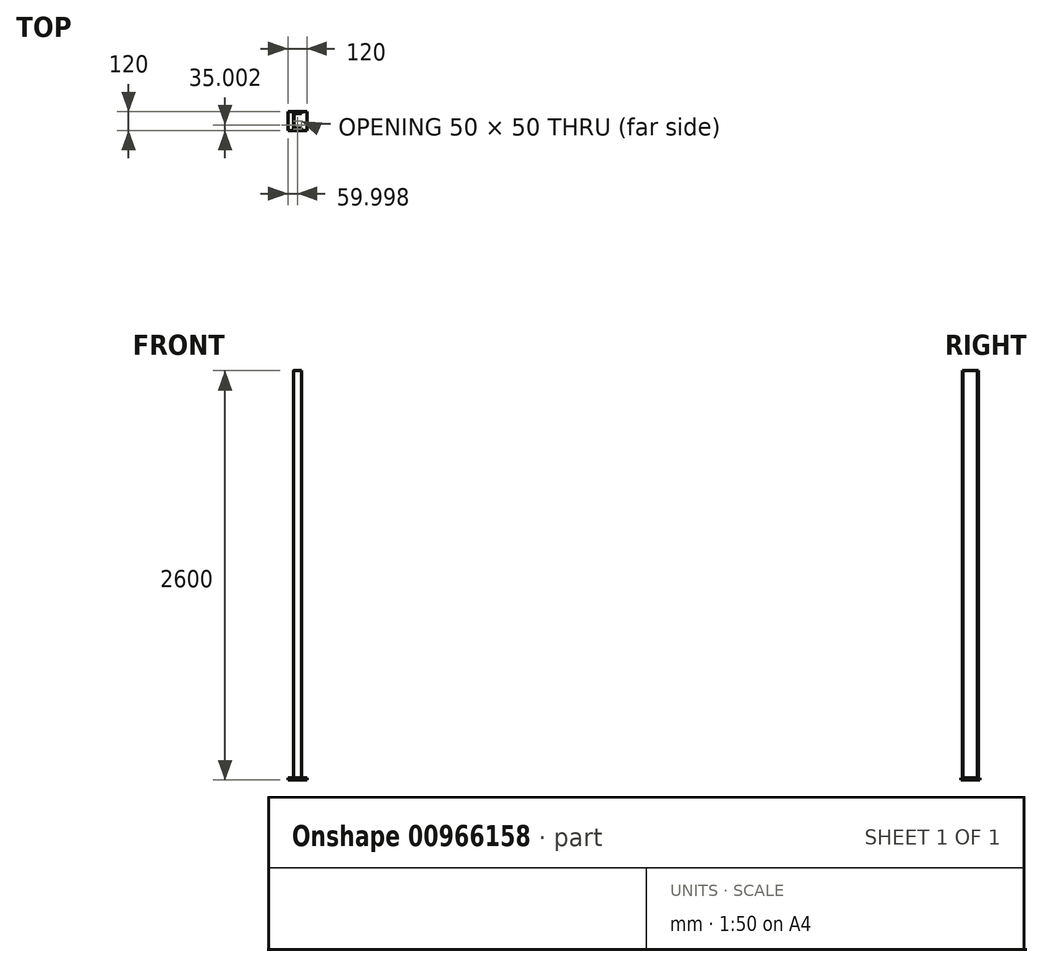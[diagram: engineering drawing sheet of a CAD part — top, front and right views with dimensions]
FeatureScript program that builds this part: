
annotation { "Feature Type Name" : "Feature", "Feature Type Description" : "" }
export const myFeature = defineFeature(function(context is Context, id is Id, definition is map)
    precondition{}
    {
        {
            var Q0;
            Q0=qCreatedBy(makeId("Top.planeOp"),FACE);
            var sketch = newSketch(context, id + "F0", { "sketchPlane" : qUnion([Q0])});
            skLineSegment(sketch, "E0.bottom", {"start": v(-5203.7, 5895.42) * mm, "end": v(-203.7, 5895.42) * mm});
            skLineSegment(sketch, "E0.top", {"start": v(-5203.7, -104.58) * mm, "end": v(-203.7, -104.58) * mm});
            skLineSegment(sketch, "E0.left", {"start": v(-5203.7, 5895.42) * mm, "end": v(-5203.7, -104.58) * mm});
            skLineSegment(sketch, "E0.right", {"start": v(-203.7, 5895.42) * mm, "end": v(-203.7, -104.58) * mm});
            skLineSegment(sketch, "E1.bottom", {"start": v(-5203.7, -104.58) * mm, "end": v(-5083.7, -104.58) * mm});
            skLineSegment(sketch, "E1.top", {"start": v(-5203.7, 15.42) * mm, "end": v(-5083.7, 15.42) * mm});
            skLineSegment(sketch, "E1.left", {"start": v(-5203.7, -104.58) * mm, "end": v(-5203.7, 15.42) * mm});
            skLineSegment(sketch, "E1.right", {"start": v(-5083.7, -104.58) * mm, "end": v(-5083.7, 15.42) * mm});
            skLineSegment(sketch, "E2", {"start": v(-5203.7, -44.58) * mm, "end": v(-5083.7, -44.58) * mm});
            skLineSegment(sketch, "E3", {"start": v(-5143.7, 5.42) * mm, "end": v(-5163.7, 5.42) * mm});
            skLineSegment(sketch, "E4", {"start": v(-5168.7, 0.42) * mm, "end": v(-5168.7, -89.58) * mm});
            skLineSegment(sketch, "E5", {"start": v(-5163.7, -94.58) * mm, "end": v(-5143.7, -94.58) * mm});
            skLineSegment(sketch, "E6", {"start": v(-5143.7, -90.58) * mm, "end": v(-5159.7, -90.58) * mm});
            skLineSegment(sketch, "E7", {"start": v(-5168.7, -90.58) * mm, "end": v(-5168.6, -90.58) * mm});
            skLineSegment(sketch, "E8", {"start": v(-5164.7, -85.58) * mm, "end": v(-5164.7, -3.58) * mm});
            skLineSegment(sketch, "E9", {"start": v(-5159.7, 1.42) * mm, "end": v(-5143.7, 1.42) * mm});
            skPoint(sketch, "E10.visualSharp", {"position": v(-5168.7, 5.42) * mm});
            skArc(sketch, "E10.filletArc", {"start": v(-5163.7, 5.42) * mm, "mid": v(-5167.24, 3.96) * mm, "end": v(-5168.7, 0.42) * mm});
            skPoint(sketch, "E11.newPointA", {"position": v(-5164.7, 5.42) * mm});
            skArc(sketch, "E11.filletArc", {"start": v(-5159.7, 1.42) * mm, "mid": v(-5163.24, -0.04) * mm, "end": v(-5164.7, -3.58) * mm});
            skPoint(sketch, "E12.newPointB", {"position": v(-5168.7, -90.58) * mm});
            skArc(sketch, "E12.filletArc", {"start": v(-5164.7, -85.58) * mm, "mid": v(-5163.24, -89.11) * mm, "end": v(-5159.7, -90.58) * mm});
            skPoint(sketch, "E13.visualSharp", {"position": v(-5168.7, -94.58) * mm});
            skArc(sketch, "E13.filletArc", {"start": v(-5168.7, -89.58) * mm, "mid": v(-5167.24, -93.11) * mm, "end": v(-5163.7, -94.58) * mm});
            skPoint(sketch, "E14.orphan", {"position": v(-5143.7, -104.58) * mm});
            skLineSegment(sketch, "E15", {"start": v(-5163.7, -94.58) * mm, "end": v(-5118.7, -94.58) * mm});
            skLineSegment(sketch, "E16", {"start": v(-5118.7, -94.58) * mm, "end": v(-5118.7, -90.58) * mm});
            skLineSegment(sketch, "E17", {"start": v(-5118.7, -90.58) * mm, "end": v(-5143.7, -90.58) * mm});
            skLineSegment(sketch, "E18", {"start": v(-5143.7, 5.42) * mm, "end": v(-5118.7, 5.42) * mm});
            skLineSegment(sketch, "E19", {"start": v(-5118.7, 5.42) * mm, "end": v(-5118.7, 1.42) * mm});
            skLineSegment(sketch, "E20", {"start": v(-5118.7, 1.42) * mm, "end": v(-5143.7, 1.42) * mm});
            skPoint(sketch, "E21.trimOffspring.end.orphan", {"position": v(-5143.7, 15.42) * mm});
            skSolve(sketch);
        }
        {
            var Q0;
            Q0=makeQuery(id+"F0.imprint","IMPRINT",FACE,{"disambiguationData":[TD([[makeQuery(id+"F0.imprint","IMPRINT",EDGE,{"derivedFrom":sQuery(id+"F0.wireOp",EDGE,"E3")}),1.0]])]});
            var Q1;
            {var subQ9=sQuery(id+"F0.wireOp",EDGE,"E5");Q1=makeQuery(id+"F0.imprint","IMPRINT",FACE,{"disambiguationData":[TD([[makeQuery(id+"F0.imprint","IMPRINT",EDGE,{"derivedFrom":subQ9}),1.0]])]});}
            extrude(context, id + "F1", {"entities" : qUnion([Q0, Q1]), "depth" : 2600 * mm, "offsetDistance" : 25 * mm});
        }
        {
            var Q0;
            {var subQ9=sQuery(id+"F0.wireOp",EDGE,"E5");Q0=makeQuery(id+"F0.imprint","IMPRINT",FACE,{"disambiguationData":[TD([[makeQuery(id+"F0.imprint","IMPRINT",EDGE,{"derivedFrom":subQ9}),1.0]])]});}
            var Q1;
            Q1=makeQuery(id+"F0.imprint","IMPRINT",FACE,{"disambiguationData":[TD([[makeQuery(id+"F0.imprint","IMPRINT",EDGE,{"derivedFrom":sQuery(id+"F0.wireOp",EDGE,"E3")}),1.0]])]});
            extrude(context, id + "F2", {"entities" : qUnion([Q0, Q1]), "operationType" : NewBodyOperationType.REMOVE, "depth" : 12 * mm, "offsetDistance" : 25 * mm});
        }
        {
            var Q0;
            {var subQ4=sQuery(id+"F0.wireOp",EDGE,"E5");Q0=makeQuery(id+"F0.imprint","IMPRINT",FACE,{"disambiguationData":[TD([[makeQuery(id+"F0.imprint","IMPRINT",EDGE,{"derivedFrom":subQ4}),-1.0]])]});}
            var Q1;
            Q1=makeQuery(id+"F0.imprint","IMPRINT",FACE,{"disambiguationData":[TD([[makeQuery(id+"F0.imprint","IMPRINT",EDGE,{"derivedFrom":sQuery(id+"F0.wireOp",EDGE,"E3")}),1.0]])]});
            var Q2;
            {var subQ9=sQuery(id+"F0.wireOp",EDGE,"E1.top");Q2=makeQuery(id+"F0.imprint","IMPRINT",FACE,{"disambiguationData":[TD([[makeQuery(id+"F0.imprint","IMPRINT",EDGE,{"derivedFrom":subQ9}),-1.0]])]});}
            extrude(context, id + "F3", {"entities" : qUnion([Q0, Q1, Q2]), "depth" : 12 * mm, "offsetDistance" : 25 * mm});
        }
    });
